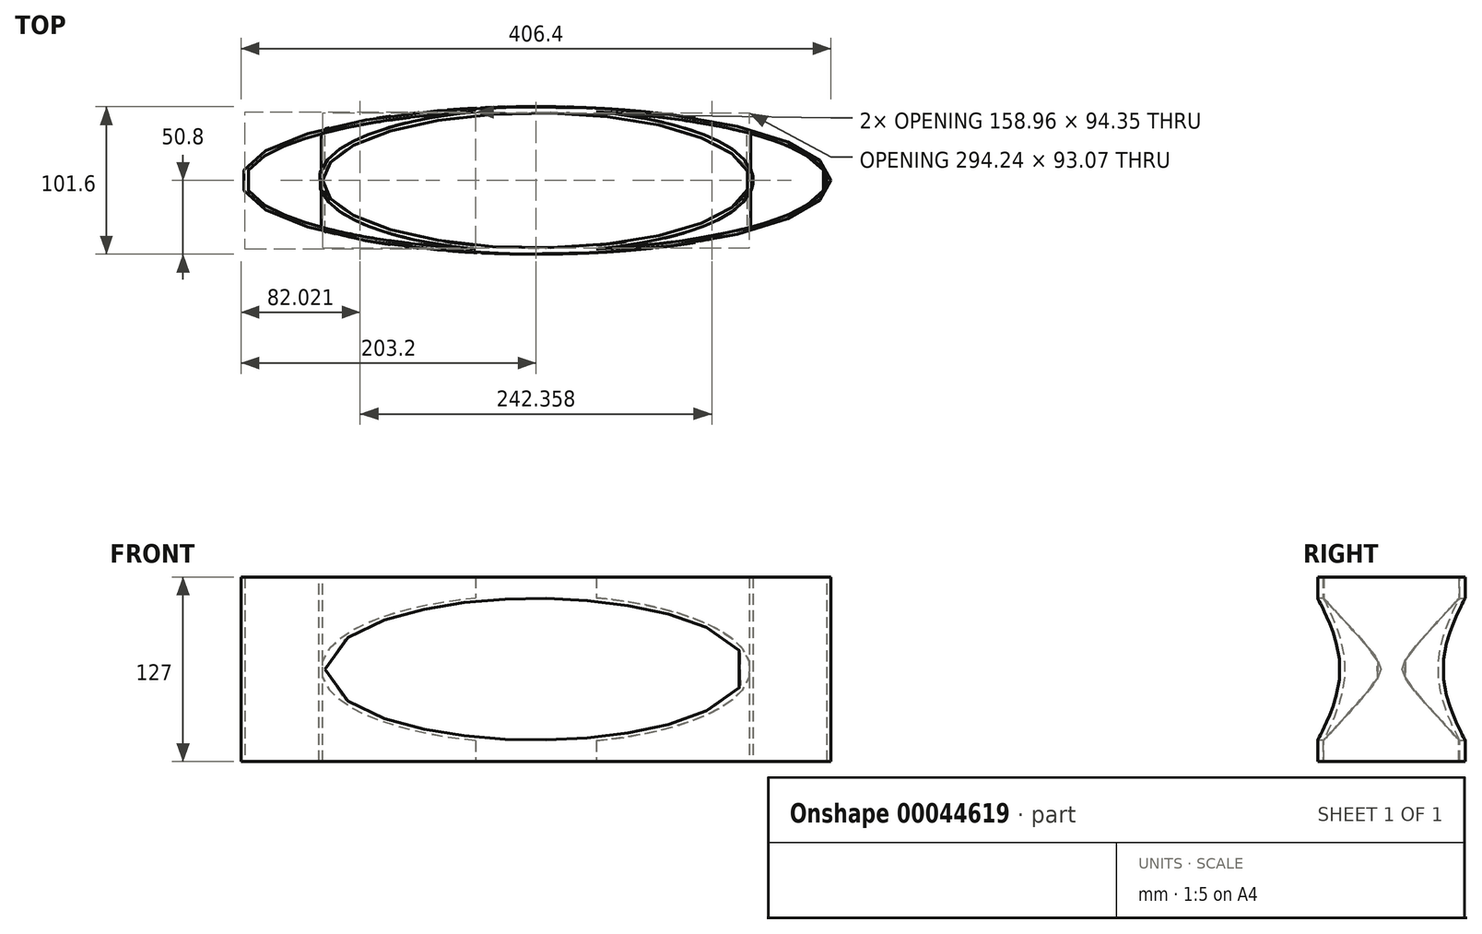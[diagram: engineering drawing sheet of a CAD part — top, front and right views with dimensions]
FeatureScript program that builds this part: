
annotation { "Feature Type Name" : "Feature", "Feature Type Description" : "" }
export const myFeature = defineFeature(function(context is Context, id is Id, definition is map)
    precondition{}
    {
        {
            var Q0;
            Q0=qCreatedBy(makeId("Top.planeOp"),FACE);
            var sketch = newSketch(context, id + "F0", { "sketchPlane" : qUnion([Q0])});
            skEllipse(sketch, "E0", {"center": v(0, 0) * mm, "majorRadius": 203.2 * mm, "minorRadius": 50.8 * mm, "majorAxis": v(1, 0)});
            skLineSegment(sketch, "E1", {"start": v(0, 0) * mm, "end": v(203.2, 0) * mm});
            skLineSegment(sketch, "E2", {"start": v(0, -50.8) * mm, "end": v(0, 0) * mm});
            skSolve(sketch);
        }
        {
            var Q0;
            {var subQ1=sQuery(id+"F0.wireOp",EDGE,"E1");Q0=makeQuery(id+"F0.imprint","IMPRINT",FACE,{"disambiguationData":[TD([[makeQuery(id+"F0.imprint","IMPRINT",EDGE,{"derivedFrom":subQ1}),-1.0]])]});}
            var Q1;
            {var subQ1=sQuery(id+"F0.wireOp",EDGE,"E1");Q1=makeQuery(id+"F0.imprint","IMPRINT",FACE,{"disambiguationData":[TD([[makeQuery(id+"F0.imprint","IMPRINT",EDGE,{"derivedFrom":subQ1}),1.0]])]});}
            extrude(context, id + "F1", {"entities" : qUnion([Q0, Q1]), "endBound" : BoundingType.SYMMETRIC, "depth" : 127 * mm});
        }
        {
            var Q0;
            Q0=qCreatedBy(makeId("Front.planeOp"),FACE);
            var sketch = newSketch(context, id + "F2", { "sketchPlane" : qUnion([Q0])});
            skEllipse(sketch, "E3", {"center": v(0, 0) * mm, "majorRadius": 145.28 * mm, "minorRadius": 48.79 * mm, "majorAxis": v(-1, 0)});
            skSolve(sketch);
        }
        {
            var Q0;
            Q0 = qSketchRegion(id + "F2", true);
            extrude(context, id + "F3", {"entities" : qUnion([Q0]), "operationType" : NewBodyOperationType.REMOVE, "endBound" : BoundingType.SYMMETRIC, "depth" : 762 * mm});
        }
        {
            var Q0;
            Q0=makeQuery(id+"F1.opExtrude","CAP_FACE",FACE,{"disambiguationData":[OSD([sQuery(id+"F0.wireOp",EDGE,"E0")])],"isStart":false});
            var sketch = newSketch(context, id + "F4", { "sketchPlane" : qUnion([Q0])});
            skEllipse(sketch, "E4", {"center": v(0, 0) * mm, "majorRadius": 46.53 * mm, "minorRadius": 147.12 * mm, "majorAxis": v(0, 1)});
            skSolve(sketch);
        }
        {
            var Q0;
            Q0 = qSketchRegion(id + "F4", true);
            extrude(context, id + "F5", {"entities" : qUnion([Q0]), "operationType" : NewBodyOperationType.REMOVE, "endBound" : BoundingType.THROUGH_ALL, "oppositeDirection" : true, "depth" : 25.4 * mm});
        }
        {
            var Q0;
            Q0=makeQuery(id+"F1.opExtrude","CAP_FACE",FACE,{"disambiguationData":[OSD([sQuery(id+"F0.wireOp",EDGE,"E0")])],"isStart":false});
            var Q1;
            Q1=makeQuery(id+"F1.opExtrude","CAP_FACE",FACE,{"disambiguationData":[OSD([sQuery(id+"F0.wireOp",EDGE,"E0")])],"isStart":true});
            shell(context, id + "F6", {"entities" : qUnion([Q0, Q1]), "thickness" : 2.54 * mm});
        }
    });
